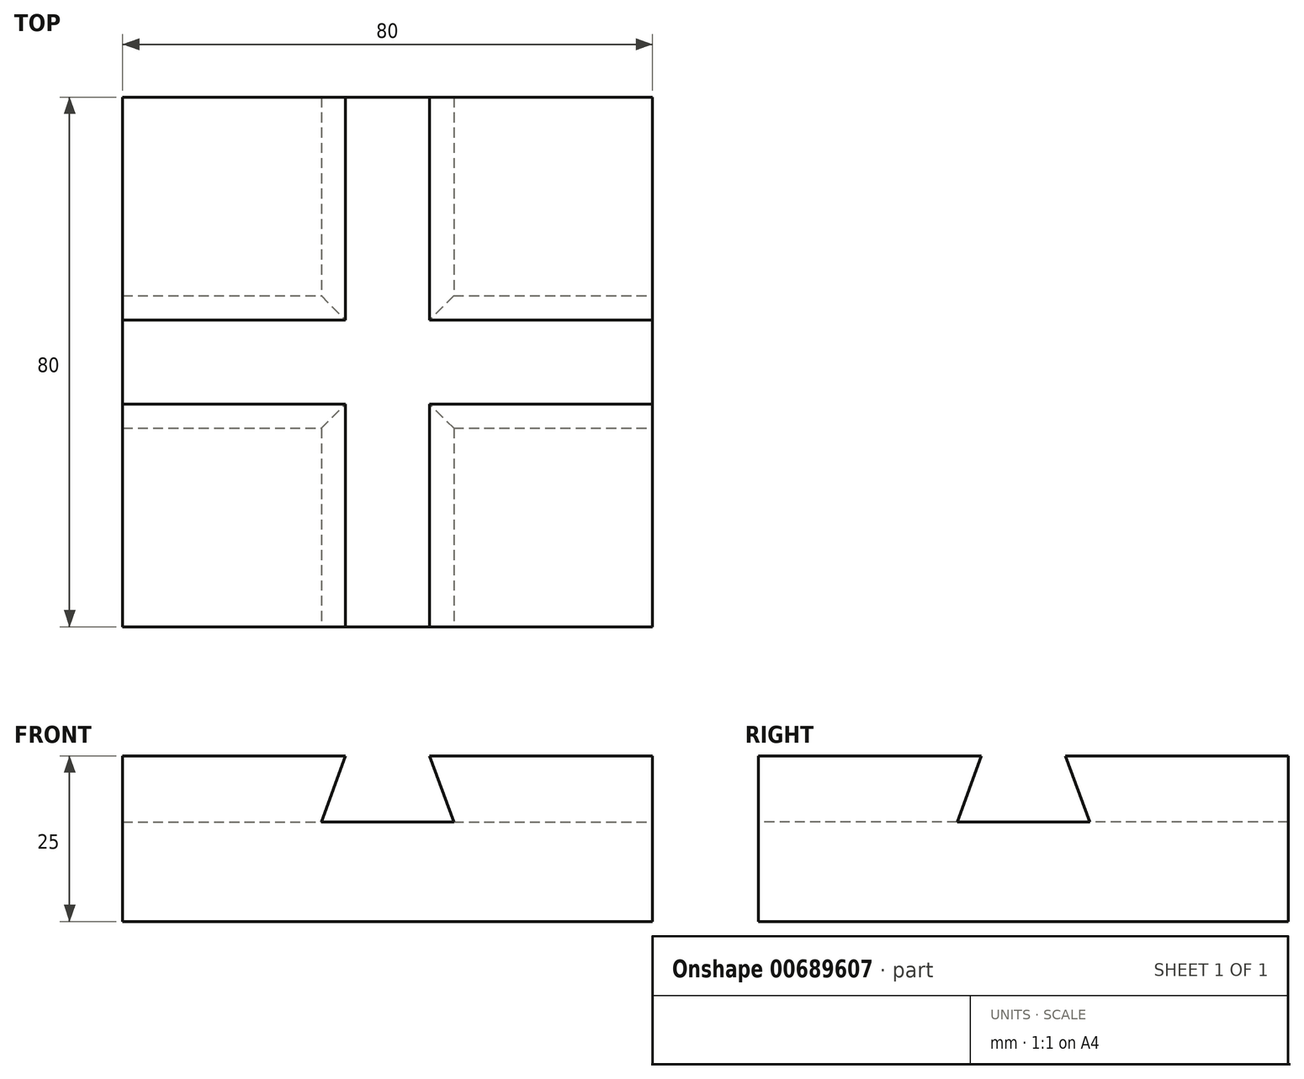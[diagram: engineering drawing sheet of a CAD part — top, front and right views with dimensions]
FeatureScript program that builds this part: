
annotation { "Feature Type Name" : "Feature", "Feature Type Description" : "" }
export const myFeature = defineFeature(function(context is Context, id is Id, definition is map)
    precondition{}
    {
        {
            var Q0;
            Q0=qCreatedBy(makeId("Front.planeOp"),FACE);
            var sketch = newSketch(context, id + "F0", { "sketchPlane" : qUnion([Q0])});
            skLineSegment(sketch, "E0.bottom", {"start": v(3.7, -5.83) * mm, "end": v(37.33, -5.83) * mm});
            skLineSegment(sketch, "E0.top", {"start": v(-42.67, -30.83) * mm, "end": v(37.33, -30.83) * mm});
            skLineSegment(sketch, "E0.left", {"start": v(-42.67, -5.83) * mm, "end": v(-42.67, -30.83) * mm});
            skLineSegment(sketch, "E0.right", {"start": v(37.33, -5.83) * mm, "end": v(37.33, -30.83) * mm});
            skLineSegment(sketch, "E1.bottom", {"start": v(7.33, -15.83) * mm, "end": v(-12.67, -15.83) * mm});
            skPoint(sketch, "E1.middle", {"position": v(-2.67, -5.83) * mm});
            skLineSegment(sketch, "E2", {"start": v(-9.03, -5.83) * mm, "end": v(-12.67, -15.83) * mm});
            skLineSegment(sketch, "E3", {"start": v(3.7, -5.83) * mm, "end": v(7.33, -15.83) * mm});
            skPoint(sketch, "E4.orphan", {"position": v(7.33, 4.17) * mm});
            skPoint(sketch, "E5.orphan", {"position": v(-12.67, 4.17) * mm});
            skLineSegment(sketch, "E6", {"start": v(-42.67, -5.83) * mm, "end": v(-9.03, -5.83) * mm});
            skSolve(sketch);
        }
        {
            var Q0;
            Q0=makeQuery(id+"F0.imprint","IMPRINT",FACE,{"disambiguationData":[TD([[makeQuery(id+"F0.imprint","IMPRINT",EDGE,{"derivedFrom":sQuery(id+"F0.wireOp",EDGE,"E0.bottom")}),-1.0]])]});
            extrude(context, id + "F1", {"entities" : qUnion([Q0]), "oppositeDirection" : true, "depth" : 80 * mm, "offsetDistance" : 25 * mm});
        }
        {
            var Q0;
            Q0=makeQuery(id+"F1.opExtrude","SWEPT_FACE",FACE,{"disambiguationData":[OSD([sQuery(id+"F0.wireOp",EDGE,"E0.right")])]});
            var sketch = newSketch(context, id + "F2", { "sketchPlane" : qUnion([Q0])});
            skLineSegment(sketch, "E7.bottom", {"start": v(50, -15.83) * mm, "end": v(30, -15.83) * mm});
            skPoint(sketch, "E7.middle", {"position": v(40, -5.83) * mm});
            skLineSegment(sketch, "E8", {"start": v(40, -5.83) * mm, "end": v(33.64, -5.83) * mm});
            skLineSegment(sketch, "E9", {"start": v(33.64, -5.83) * mm, "end": v(30, -15.83) * mm});
            skLineSegment(sketch, "E10", {"start": v(40, -5.83) * mm, "end": v(46.36, -5.83) * mm});
            skLineSegment(sketch, "E11", {"start": v(46.36, -5.83) * mm, "end": v(50, -15.83) * mm});
            skPoint(sketch, "E7.left.end.orphan", {"position": v(50, 4.17) * mm});
            skPoint(sketch, "E7.right.end.orphan", {"position": v(30, 4.17) * mm});
            skSolve(sketch);
        }
        {
            var Q0;
            Q0=makeQuery(id+"F2.imprint","IMPRINT",FACE,{"disambiguationData":[TD([[makeQuery(id+"F2.imprint","IMPRINT",EDGE,{"derivedFrom":sQuery(id+"F2.wireOp",EDGE,"E7.bottom")}),-1.0]])]});
            extrude(context, id + "F3", {"entities" : qUnion([Q0]), "operationType" : NewBodyOperationType.REMOVE, "oppositeDirection" : true, "depth" : 80 * mm, "offsetDistance" : 25 * mm});
        }
    });
